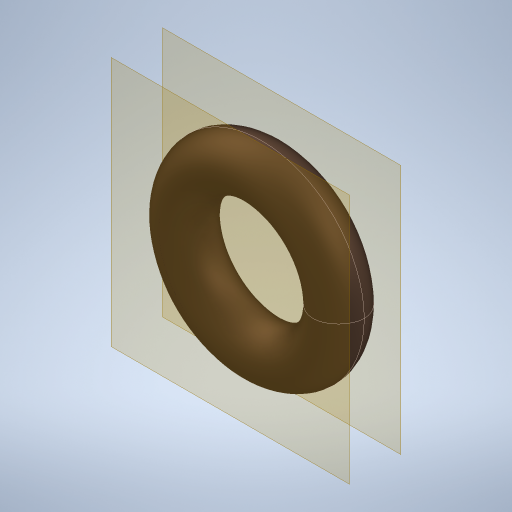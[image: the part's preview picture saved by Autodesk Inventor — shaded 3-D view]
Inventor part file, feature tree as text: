
AUTODESK INVENTOR PART (.ipt)
format: ipt  version: 2024 (Build 280153000, 153)  size: 327,168 bytes
history: native  units: in
note: dims shown in document units (in); Inventor stores cm internally (conversion verified against a paired STEP export)
features: plane x2, other x1
ambient origin geometry x8: Origin, YZ Plane, XZ Plane, XY Plane, X Axis, Y Axis, Z Axis, Center Point
bodies: Solid1 (feature_tree)
feature tree (3):
  other  "Form1"
  plane  "Work Plane1"
  plane  "Work Plane2"
